# Revit family: AISC Angle Shapes-Top
name_source: partatom
category: Detail Items
revit_build: Autodesk Revit Architecture 2012 (Build: 20110210_1515)
units: mm (PartAtom-declared; Revit-internal decimal feet)

## types (127) — shared parameters
Keynote = 05 12 00.A0

## per-type parameters (varying)
| type | A | W | b | d | k | t | x | y |
| L8X8X1-1/8 | 0.12 SF | 56.9 | 0' - 8" | 0' - 8" | 0' - 1 3/4" | 0' - 1 1/8" | 0' - 2 13/32" | 0' - 2 13/32" |
| L8X8X1 | 0.1 SF | 51 | 0' - 8" | 0' - 8" | 0' - 1 5/8" | 0' - 1" | 0' - 2 3/8" | 0' - 2 3/8" |
| L8X8X7/8 | 0.09 SF | 45 | 0' - 8" | 0' - 8" | 0' - 1 1/2" | 0' - 0 7/8" | 0' - 2 5/16" | 0' - 2 5/16" |
| L8X8X3/4 | 0.08 SF | 38.9 | 0' - 8" | 0' - 8" | 0' - 1 3/8" | 0' - 0 3/4" | 0' - 2 1/4" | 0' - 2 1/4" |
| L8X8X5/8 | 0.07 SF | 32.7 | 0' - 8" | 0' - 8" | 0' - 1 1/4" | 0' - 0 5/8" | 0' - 2 7/32" | 0' - 2 7/32" |
| L8X8X9/16 | 0.06 SF | 29.6 | 0' - 8" | 0' - 8" | 0' - 1 3/16" | 0' - 0 9/16" | 0' - 2 3/16" | 0' - 2 3/16" |
| L8X8X1/2 | 0.05 SF | 26.4 | 0' - 8" | 0' - 8" | 0' - 1 1/8" | 0' - 0 1/2" | 0' - 2 5/32" | 0' - 2 5/32" |
| L8X6X1 | 0.09 SF | 44.2 | 0' - 6" | 0' - 8" | 0' - 1 1/2" | 0' - 1" | 0' - 1 21/32" | 0' - 2 21/32" |
| L8X6X7/8 | 0.08 SF | 39.1 | 0' - 6" | 0' - 8" | 0' - 1 3/8" | 0' - 0 7/8" | 0' - 1 19/32" | 0' - 2 19/32" |
| L8X6X3/4 | 0.07 SF | 33.8 | 0' - 6" | 0' - 8" | 0' - 1 1/4" | 0' - 0 3/4" | 0' - 1 9/16" | 0' - 2 9/16" |
| L8X6X5/8 | 0.06 SF | 28.5 | 0' - 6" | 0' - 8" | 0' - 1 1/8" | 0' - 0 5/8" | 0' - 1 1/2" | 0' - 2 1/2" |
| L8X6X9/16 | 0.05 SF | 25.7 | 0' - 6" | 0' - 8" | 0' - 1 1/16" | 0' - 0 9/16" | 0' - 1 1/2" | 0' - 2 15/32" |
| L8X6X1/2 | 0.05 SF | 23 | 0' - 6" | 0' - 8" | 0' - 1" | 0' - 0 1/2" | 0' - 1 15/32" | 0' - 2 15/32" |
| L8X6X7/16 | 0.04 SF | 20.2 | 0' - 6" | 0' - 8" | 0' - 0 15/16" | 0' - 0 7/16" | 0' - 1 7/16" | 0' - 2 7/16" |
| L8X4X1 | 0.08 SF | 37.4 | 0' - 4" | 0' - 8" | 0' - 1 1/2" | 0' - 1" | 0' - 1 1/32" | 0' - 3 1/32" |
| L8X4X7/8 | 0.07 SF | 33.1 | 0' - 4" | 0' - 8" | 0' - 1 3/8" | 0' - 0 7/8" | 0' - 1" | 0' - 3" |
| L8X4X3/4 | 0.06 SF | 28.7 | 0' - 4" | 0' - 8" | 0' - 1 1/4" | 0' - 0 3/4" | 0' - 0 15/16" | 0' - 2 15/16" |
| L8X4X5/8 | 0.05 SF | 24.2 | 0' - 4" | 0' - 8" | 0' - 1 1/8" | 0' - 0 5/8" | 0' - 0 29/32" | 0' - 2 7/8" |
| L8X4X9/16 | 0.04 SF | 21.9 | 0' - 4" | 0' - 8" | 0' - 1 1/16" | 0' - 0 9/16" | 0' - 0 7/8" | 0' - 2 7/8" |
| L8X4X1/2 | 0.04 SF | 19.6 | 0' - 4" | 0' - 8" | 0' - 1" | 0' - 0 1/2" | 0' - 0 27/32" | 0' - 2 27/32" |
| L8X4X7/16 | 0.04 SF | 17.2 | 0' - 4" | 0' - 8" | 0' - 0 15/16" | 0' - 0 7/16" | 0' - 0 27/32" | 0' - 2 13/16" |
| L7X4X3/4 | 0.05 SF | 26.2 | 0' - 4" | 0' - 7" | 0' - 1 1/4" | 0' - 0 3/4" | 0' - 1" | 0' - 2 1/2" |
| L7X4X5/8 | 0.05 SF | 22.1 | 0' - 4" | 0' - 7" | 0' - 1 1/8" | 0' - 0 5/8" | 0' - 0 31/32" | 0' - 2 7/16" |
| L7X4X1/2 | 0.04 SF | 17.9 | 0' - 4" | 0' - 7" | 0' - 1" | 0' - 0 1/2" | 0' - 0 29/32" | 0' - 2 13/32" |
| L7X4X7/16 | 0.03 SF | 15.7 | 0' - 4" | 0' - 7" | 0' - 0 15/16" | 0' - 0 7/16" | 0' - 0 7/8" | 0' - 2 3/8" |
| L7X4X3/8 | 0.03 SF | 13.6 | 0' - 4" | 0' - 7" | 0' - 0 7/8" | 0' - 0 3/8" | 0' - 0 7/8" | 0' - 2 11/32" |
| L6X6X1 | 0.08 SF | 37.4 | 0' - 6" | 0' - 6" | 0' - 1 1/2" | 0' - 1" | 0' - 1 7/8" | 0' - 1 7/8" |
| L6X6X7/8 | 0.07 SF | 33.1 | 0' - 6" | 0' - 6" | 0' - 1 3/8" | 0' - 0 7/8" | 0' - 1 13/16" | 0' - 1 13/16" |
| L6X6X3/4 | 0.06 SF | 28.7 | 0' - 6" | 0' - 6" | 0' - 1 1/4" | 0' - 0 3/4" | 0' - 1 25/32" | 0' - 1 25/32" |
| L6X6X5/8 | 0.05 SF | 24.2 | 0' - 6" | 0' - 6" | 0' - 1 1/8" | 0' - 0 5/8" | 0' - 1 23/32" | 0' - 1 23/32" |
| L6X6X9/16 | 0.04 SF | 21.9 | 0' - 6" | 0' - 6" | 0' - 1 1/16" | 0' - 0 9/16" | 0' - 1 11/16" | 0' - 1 11/16" |
| L6X6X1/2 | 0.04 SF | 19.6 | 0' - 6" | 0' - 6" | 0' - 1" | 0' - 0 1/2" | 0' - 1 21/32" | 0' - 1 21/32" |
| L6X6X7/16 | 0.04 SF | 17.2 | 0' - 6" | 0' - 6" | 0' - 0 15/16" | 0' - 0 7/16" | 0' - 1 21/32" | 0' - 1 21/32" |
| L6X6X3/8 | 0.03 SF | 14.9 | 0' - 6" | 0' - 6" | 0' - 0 7/8" | 0' - 0 3/8" | 0' - 1 5/8" | 0' - 1 5/8" |
| L6X6X5/16 | 0.03 SF | 12.4 | 0' - 6" | 0' - 6" | 0' - 0 13/16" | 0' - 0 5/16" | 0' - 1 19/32" | 0' - 1 19/32" |
| L6X4X7/8 | 0.06 SF | 27.2 | 0' - 4" | 0' - 6" | 0' - 1 3/8" | 0' - 0 7/8" | 0' - 1 1/8" | 0' - 2 1/8" |
| L6X4X3/4 | 0.05 SF | 23.6 | 0' - 4" | 0' - 6" | 0' - 1 1/4" | 0' - 0 3/4" | 0' - 1 1/16" | 0' - 2 1/16" |
| L6X4X5/8 | 0.04 SF | 20 | 0' - 4" | 0' - 6" | 0' - 1 1/8" | 0' - 0 5/8" | 0' - 1 1/32" | 0' - 2 1/32" |
| L6X4X9/16 | 0.04 SF | 18.1 | 0' - 4" | 0' - 6" | 0' - 1 1/16" | 0' - 0 9/16" | 0' - 1" | 0' - 2" |
| L6X4X1/2 | 0.03 SF | 16.2 | 0' - 4" | 0' - 6" | 0' - 1" | 0' - 0 1/2" | 0' - 0 31/32" | 0' - 1 31/32" |
| L6X4X7/16 | 0.03 SF | 14.3 | 0' - 4" | 0' - 6" | 0' - 0 15/16" | 0' - 0 7/16" | 0' - 0 31/32" | 0' - 1 15/16" |
| L6X4X3/8 | 0.03 SF | 12.3 | 0' - 4" | 0' - 6" | 0' - 0 7/8" | 0' - 0 3/8" | 0' - 0 15/16" | 0' - 1 15/16" |
| L6X4X5/16 | 0.02 SF | 10.3 | 0' - 4" | 0' - 6" | 0' - 0 13/16" | 0' - 0 5/16" | 0' - 0 29/32" | 0' - 1 29/32" |
| L6X3-1/2X1/2 | 0.03 SF | 15.3 | 0' - 3 1/2" | 0' - 6" | 0' - 1" | 0' - 0 1/2" | 0' - 0 27/32" | 0' - 2 1/16" |
| L6X3-1/2X3/8 | 0.02 SF | 11.7 | 0' - 3 1/2" | 0' - 6" | 0' - 0 7/8" | 0' - 0 3/8" | 0' - 0 25/32" | 0' - 2 1/32" |
| L6X3-1/2X5/16 | 0.02 SF | 9.8 | 0' - 3 1/2" | 0' - 6" | 0' - 0 13/16" | 0' - 0 5/16" | 0' - 0 3/4" | 0' - 2" |
| L5X5X7/8 | 0.06 SF | 27.2 | 0' - 5" | 0' - 5" | 0' - 1 3/8" | 0' - 0 7/8" | 0' - 1 9/16" | 0' - 1 9/16" |
| L5X5X3/4 | 0.05 SF | 23.6 | 0' - 5" | 0' - 5" | 0' - 1 1/4" | 0' - 0 3/4" | 0' - 1 17/32" | 0' - 1 17/32" |
| L5X5X5/8 | 0.04 SF | 20 | 0' - 5" | 0' - 5" | 0' - 1 1/8" | 0' - 0 5/8" | 0' - 1 15/32" | 0' - 1 15/32" |
| L5X5X1/2 | 0.03 SF | 16.2 | 0' - 5" | 0' - 5" | 0' - 1" | 0' - 0 1/2" | 0' - 1 13/32" | 0' - 1 13/32" |
| L5X5X7/16 | 0.03 SF | 14.3 | 0' - 5" | 0' - 5" | 0' - 0 15/16" | 0' - 0 7/16" | 0' - 1 13/32" | 0' - 1 13/32" |
| L5X5X3/8 | 0.03 SF | 12.3 | 0' - 5" | 0' - 5" | 0' - 0 7/8" | 0' - 0 3/8" | 0' - 1 3/8" | 0' - 1 3/8" |
| L5X5X5/16 | 0.02 SF | 10.3 | 0' - 5" | 0' - 5" | 0' - 0 13/16" | 0' - 0 5/16" | 0' - 1 11/32" | 0' - 1 11/32" |
| L5X3-1/2X3/4 | 0.04 SF | 19.8 | 0' - 3 1/2" | 0' - 5" | 0' - 1 3/16" | 0' - 0 3/4" | 0' - 1" | 0' - 1 3/4" |
| L5X3-1/2X5/8 | 0.03 SF | 16.8 | 0' - 3 1/2" | 0' - 5" | 0' - 1 1/16" | 0' - 0 5/8" | 0' - 0 15/16" | 0' - 1 11/16" |
| L5X3-1/2X1/2 | 0.03 SF | 13.6 | 0' - 3 1/2" | 0' - 5" | 0' - 0 15/16" | 0' - 0 1/2" | 0' - 0 29/32" | 0' - 1 21/32" |
| L5X3-1/2X3/8 | 0.02 SF | 10.4 | 0' - 3 1/2" | 0' - 5" | 0' - 0 13/16" | 0' - 0 3/8" | 0' - 0 27/32" | 0' - 1 19/32" |
| L5X3-1/2X5/16 | 0.02 SF | 8.7 | 0' - 3 1/2" | 0' - 5" | 0' - 0 3/4" | 0' - 0 5/16" | 0' - 0 27/32" | 0' - 1 9/16" |
| L5X3-1/2X1/4 | 0.01 SF | 7 | 0' - 3 1/2" | 0' - 5" | 0' - 0 11/16" | 0' - 0 1/4" | 0' - 0 13/16" | 0' - 1 9/16" |
| L5X3X1/2 | 0.03 SF | 12.8 | 0' - 3" | 0' - 5" | 0' - 0 15/16" | 0' - 0 1/2" | 0' - 0 3/4" | 0' - 1 3/4" |
| L5X3X7/16 | 0.02 SF | 11.3 | 0' - 3" | 0' - 5" | 0' - 0 7/8" | 0' - 0 7/16" | 0' - 0 23/32" | 0' - 1 23/32" |
| L5X3X3/8 | 0.02 SF | 9.8 | 0' - 3" | 0' - 5" | 0' - 0 13/16" | 0' - 0 3/8" | 0' - 0 11/16" | 0' - 1 11/16" |
| L5X3X5/16 | 0.02 SF | 8.2 | 0' - 3" | 0' - 5" | 0' - 0 3/4" | 0' - 0 5/16" | 0' - 0 11/16" | 0' - 1 21/32" |
| L5X3X1/4 | 0.01 SF | 6.6 | 0' - 3" | 0' - 5" | 0' - 0 11/16" | 0' - 0 1/4" | 0' - 0 21/32" | 0' - 1 5/8" |
| L4X4X3/4 | 0.04 SF | 18.5 | 0' - 4" | 0' - 4" | 0' - 1 1/8" | 0' - 0 3/4" | 0' - 1 9/32" | 0' - 1 9/32" |
| L4X4X5/8 | 0.03 SF | 15.7 | 0' - 4" | 0' - 4" | 0' - 1" | 0' - 0 5/8" | 0' - 1 7/32" | 0' - 1 7/32" |
| L4X4X1/2 | 0.03 SF | 12.8 | 0' - 4" | 0' - 4" | 0' - 0 7/8" | 0' - 0 1/2" | 0' - 1 3/16" | 0' - 1 3/16" |
| L4X4X7/16 | 0.02 SF | 11.3 | 0' - 4" | 0' - 4" | 0' - 0 13/16" | 0' - 0 7/16" | 0' - 1 5/32" | 0' - 1 5/32" |
| L4X4X3/8 | 0.02 SF | 9.8 | 0' - 4" | 0' - 4" | 0' - 0 3/4" | 0' - 0 3/8" | 0' - 1 1/8" | 0' - 1 1/8" |
| L4X4X5/16 | 0.02 SF | 8.2 | 0' - 4" | 0' - 4" | 0' - 0 11/16" | 0' - 0 5/16" | 0' - 1 1/8" | 0' - 1 1/8" |
| L4X4X1/4 | 0.01 SF | 6.6 | 0' - 4" | 0' - 4" | 0' - 0 5/8" | 0' - 0 1/4" | 0' - 1 3/32" | 0' - 1 3/32" |
| L4X3-1/2X1/2 | 0.02 SF | 11.9 | 0' - 3 1/2" | 0' - 4" | 0' - 0 7/8" | 0' - 0 1/2" | 0' - 1" | 0' - 1 1/4" |
| L4X3-1/2X3/8 | 0.02 SF | 9.1 | 0' - 3 1/2" | 0' - 4" | 0' - 0 3/4" | 0' - 0 3/8" | 0' - 0 15/16" | 0' - 1 3/16" |
| L4X3-1/2X5/16 | 0.02 SF | 7.7 | 0' - 3 1/2" | 0' - 4" | 0' - 0 11/16" | 0' - 0 5/16" | 0' - 0 15/16" | 0' - 1 5/32" |
| L4X3-1/2X1/4 | 0.01 SF | 6.2 | 0' - 3 1/2" | 0' - 4" | 0' - 0 5/8" | 0' - 0 1/4" | 0' - 0 29/32" | 0' - 1 1/8" |
| L4X3X5/8 | 0.03 SF | 13.6 | 0' - 3" | 0' - 4" | 0' - 1" | 0' - 0 5/8" | 0' - 0 7/8" | 0' - 1 3/8" |
| L4X3X1/2 | 0.02 SF | 11.1 | 0' - 3" | 0' - 4" | 0' - 0 7/8" | 0' - 0 1/2" | 0' - 0 13/16" | 0' - 1 5/16" |
| L4X3X3/8 | 0.02 SF | 8.5 | 0' - 3" | 0' - 4" | 0' - 0 3/4" | 0' - 0 3/8" | 0' - 0 25/32" | 0' - 1 9/32" |
| L4X3X5/16 | 0.01 SF | 7.2 | 0' - 3" | 0' - 4" | 0' - 0 11/16" | 0' - 0 5/16" | 0' - 0 3/4" | 0' - 1 1/4" |
| L4X3X1/4 | 0.01 SF | 5.8 | 0' - 3" | 0' - 4" | 0' - 0 5/8" | 0' - 0 1/4" | 0' - 0 23/32" | 0' - 1 7/32" |
| L3-1/2X3-1/2X1/2 | 0.02 SF | 11.1 | 0' - 3 1/2" | 0' - 3 1/2" | 0' - 0 7/8" | 0' - 0 1/2" | 0' - 1 1/16" | 0' - 1 1/16" |
| L3-1/2X3-1/2X7/16 | 0.02 SF | 9.8 | 0' - 3 1/2" | 0' - 3 1/2" | 0' - 0 13/16" | 0' - 0 7/16" | 0' - 1 1/32" | 0' - 1 1/32" |
| L3-1/2X3-1/2X3/8 | 0.02 SF | 8.5 | 0' - 3 1/2" | 0' - 3 1/2" | 0' - 0 3/4" | 0' - 0 3/8" | 0' - 1" | 0' - 1" |
| L3-1/2X3-1/2X5/16 | 0.01 SF | 7.2 | 0' - 3 1/2" | 0' - 3 1/2" | 0' - 0 11/16" | 0' - 0 5/16" | 0' - 0 31/32" | 0' - 0 31/32" |
| L3-1/2X3-1/2X1/4 | 0.01 SF | 5.8 | 0' - 3 1/2" | 0' - 3 1/2" | 0' - 0 5/8" | 0' - 0 1/4" | 0' - 0 31/32" | 0' - 0 31/32" |
| L3-1/2X3X1/2 | 0.02 SF | 10.2 | 0' - 3" | 0' - 3 1/2" | 0' - 0 7/8" | 0' - 0 1/2" | 0' - 0 7/8" | 0' - 1 1/8" |
| L3-1/2X3X7/16 | 0.02 SF | 9.1 | 0' - 3" | 0' - 3 1/2" | 0' - 0 13/16" | 0' - 0 7/16" | 0' - 0 27/32" | 0' - 1 3/32" |
| L3-1/2X3X3/8 | 0.02 SF | 7.9 | 0' - 3" | 0' - 3 1/2" | 0' - 0 3/4" | 0' - 0 3/8" | 0' - 0 13/16" | 0' - 1 1/16" |
| L3-1/2X3X5/16 | 0.01 SF | 6.6 | 0' - 3" | 0' - 3 1/2" | 0' - 0 11/16" | 0' - 0 5/16" | 0' - 0 13/16" | 0' - 1 1/16" |
| L3-1/2X3X1/4 | 0.01 SF | 5.4 | 0' - 3" | 0' - 3 1/2" | 0' - 0 5/8" | 0' - 0 1/4" | 0' - 0 25/32" | 0' - 1 1/32" |
| L3-1/2X2-1/2X1/2 | 0.02 SF | 9.4 | 0' - 2 1/2" | 0' - 3 1/2" | 0' - 0 7/8" | 0' - 0 1/2" | 0' - 0 11/16" | 0' - 1 3/16" |
| L3-1/2X2-1/2X3/8 | 0.01 SF | 7.2 | 0' - 2 1/2" | 0' - 3 1/2" | 0' - 0 3/4" | 0' - 0 3/8" | 0' - 0 21/32" | 0' - 1 5/32" |
| L3-1/2X2-1/2X5/16 | 0.01 SF | 6.1 | 0' - 2 1/2" | 0' - 3 1/2" | 0' - 0 11/16" | 0' - 0 5/16" | 0' - 0 5/8" | 0' - 1 1/8" |
| L3-1/2X2-1/2X1/4 | 0.01 SF | 4.9 | 0' - 2 1/2" | 0' - 3 1/2" | 0' - 0 5/8" | 0' - 0 1/4" | 0' - 0 19/32" | 0' - 1 3/32" |
| L3X3X1/2 | 0.02 SF | 9.4 | 0' - 3" | 0' - 3" | 0' - 0 7/8" | 0' - 0 1/2" | 0' - 0 15/16" | 0' - 0 15/16" |
| L3X3X7/16 | 0.02 SF | 8.3 | 0' - 3" | 0' - 3" | 0' - 0 13/16" | 0' - 0 7/16" | 0' - 0 29/32" | 0' - 0 29/32" |
| L3X3X3/8 | 0.01 SF | 7.2 | 0' - 3" | 0' - 3" | 0' - 0 3/4" | 0' - 0 3/8" | 0' - 0 7/8" | 0' - 0 7/8" |
| L3X3X5/16 | 0.01 SF | 6.1 | 0' - 3" | 0' - 3" | 0' - 0 11/16" | 0' - 0 5/16" | 0' - 0 7/8" | 0' - 0 7/8" |
| L3X3X1/4 | 0.01 SF | 4.9 | 0' - 3" | 0' - 3" | 0' - 0 5/8" | 0' - 0 1/4" | 0' - 0 27/32" | 0' - 0 27/32" |
| L3X3X3/16 | 0.01 SF | 3.71 | 0' - 3" | 0' - 3" | 0' - 0 9/16" | 0' - 0 3/16" | 0' - 0 13/16" | 0' - 0 13/16" |
| L3X2-1/2X1/2 | 0.02 SF | 8.5 | 0' - 2 1/2" | 0' - 3" | 0' - 0 7/8" | 0' - 0 1/2" | 0' - 0 3/4" | 0' - 1" |
| L3X2-1/2X7/16 | 0.02 SF | 7.6 | 0' - 2 1/2" | 0' - 3" | 0' - 0 13/16" | 0' - 0 7/16" | 0' - 0 23/32" | 0' - 0 31/32" |
| L3X2-1/2X3/8 | 0.01 SF | 6.6 | 0' - 2 1/2" | 0' - 3" | 0' - 0 3/4" | 0' - 0 3/8" | 0' - 0 11/16" | 0' - 0 15/16" |
| L3X2-1/2X5/16 | 0.01 SF | 5.6 | 0' - 2 1/2" | 0' - 3" | 0' - 0 11/16" | 0' - 0 5/16" | 0' - 0 11/16" | 0' - 0 15/16" |
| L3X2-1/2X1/4 | 0.01 SF | 4.5 | 0' - 2 1/2" | 0' - 3" | 0' - 0 5/8" | 0' - 0 1/4" | 0' - 0 21/32" | 0' - 0 29/32" |
| L3X2-1/2X3/16 | 0.01 SF | 3.39 | 0' - 2 1/2" | 0' - 3" | 0' - 0 9/16" | 0' - 0 3/16" | 0' - 0 5/8" | 0' - 0 7/8" |
| L3X2X1/2 | 0.02 SF | 7.7 | 0' - 2" | 0' - 3" | 0' - 0 13/16" | 0' - 0 1/2" | 0' - 0 19/32" | 0' - 1 3/32" |
| L3X2X3/8 | 0.01 SF | 5.9 | 0' - 2" | 0' - 3" | 0' - 0 11/16" | 0' - 0 3/8" | 0' - 0 17/32" | 0' - 1 1/32" |
| L3X2X5/16 | 0.01 SF | 5 | 0' - 2" | 0' - 3" | 0' - 0 5/8" | 0' - 0 5/16" | 0' - 0 1/2" | 0' - 1" |
| L3X2X1/4 | 0.01 SF | 4.1 | 0' - 2" | 0' - 3" | 0' - 0 9/16" | 0' - 0 1/4" | 0' - 0 1/2" | 0' - 0 31/32" |
| L3X2X3/16 | 0.01 SF | 3.07 | 0' - 2" | 0' - 3" | 0' - 0 1/2" | 0' - 0 3/16" | 0' - 0 15/32" | 0' - 0 15/16" |
| L2-1/2X2-1/2X1/2 | 0.02 SF | 7.7 | 0' - 2 1/2" | 0' - 2 1/2" | 0' - 0 3/4" | 0' - 0 1/2" | 0' - 0 13/16" | 0' - 0 13/16" |
| L2-1/2X2-1/2X3/8 | 0.01 SF | 5.9 | 0' - 2 1/2" | 0' - 2 1/2" | 0' - 0 5/8" | 0' - 0 3/8" | 0' - 0 3/4" | 0' - 0 3/4" |
| L2-1/2X2-1/2X5/16 | 0.01 SF | 5 | 0' - 2 1/2" | 0' - 2 1/2" | 0' - 0 9/16" | 0' - 0 5/16" | 0' - 0 3/4" | 0' - 0 3/4" |
| L2-1/2X2-1/2X1/4 | 0.01 SF | 4.1 | 0' - 2 1/2" | 0' - 2 1/2" | 0' - 0 1/2" | 0' - 0 1/4" | 0' - 0 23/32" | 0' - 0 23/32" |
| L2-1/2X2-1/2X3/16 | 0.01 SF | 3.07 | 0' - 2 1/2" | 0' - 2 1/2" | 0' - 0 7/16" | 0' - 0 3/16" | 0' - 0 11/16" | 0' - 0 11/16" |
| L2-1/2X2X3/8 | 0.01 SF | 5.3 | 0' - 2" | 0' - 2 1/2" | 0' - 0 5/8" | 0' - 0 3/8" | 0' - 0 9/16" | 0' - 0 13/16" |
| L2-1/2X2X5/16 | 0.01 SF | 4.5 | 0' - 2" | 0' - 2 1/2" | 0' - 0 9/16" | 0' - 0 5/16" | 0' - 0 9/16" | 0' - 0 13/16" |
| L2-1/2X2X1/4 | 0.01 SF | 3.62 | 0' - 2" | 0' - 2 1/2" | 0' - 0 1/2" | 0' - 0 1/4" | 0' - 0 17/32" | 0' - 0 25/32" |
| L2-1/2X2X3/16 | 0.01 SF | 2.75 | 0' - 2" | 0' - 2 1/2" | 0' - 0 7/16" | 0' - 0 3/16" | 0' - 0 1/2" | 0' - 0 3/4" |
| L2-1/2X1-1/2X1/4 | 0.01 SF | 3.22 | 0' - 1 1/2" | 0' - 2 1/2" | 0' - 0 1/2" | 0' - 0 1/4" | 0' - 0 3/8" | 0' - 0 7/8" |
| L2-1/2X1-1/2X3/16 | 0 SF | 2.47 | 0' - 1 1/2" | 0' - 2 1/2" | 0' - 0 7/16" | 0' - 0 3/16" | 0' - 0 11/32" | 0' - 0 27/32" |
| L2X2X3/8 | 0.01 SF | 4.7 | 0' - 2" | 0' - 2" | 0' - 0 5/8" | 0' - 0 3/8" | 0' - 0 5/8" | 0' - 0 5/8" |
| L2X2X5/16 | 0.01 SF | 3.92 | 0' - 2" | 0' - 2" | 0' - 0 9/16" | 0' - 0 5/16" | 0' - 0 19/32" | 0' - 0 19/32" |
| L2X2X1/4 | 0.01 SF | 3.19 | 0' - 2" | 0' - 2" | 0' - 0 1/2" | 0' - 0 1/4" | 0' - 0 19/32" | 0' - 0 19/32" |
| L2X2X3/16 | 0 SF | 2.44 | 0' - 2" | 0' - 2" | 0' - 0 7/16" | 0' - 0 3/16" | 0' - 0 9/16" | 0' - 0 9/16" |
| L2X2X1/8 | 0 SF | 1.65 | 0' - 2" | 0' - 2" | 0' - 0 3/8" | 0' - 0 1/8" | 0' - 0 17/32" | 0' - 0 17/32" |

## geometry (parser evidence)
native form markers: Sweep x1
no freeform markers — native parametric forms only
